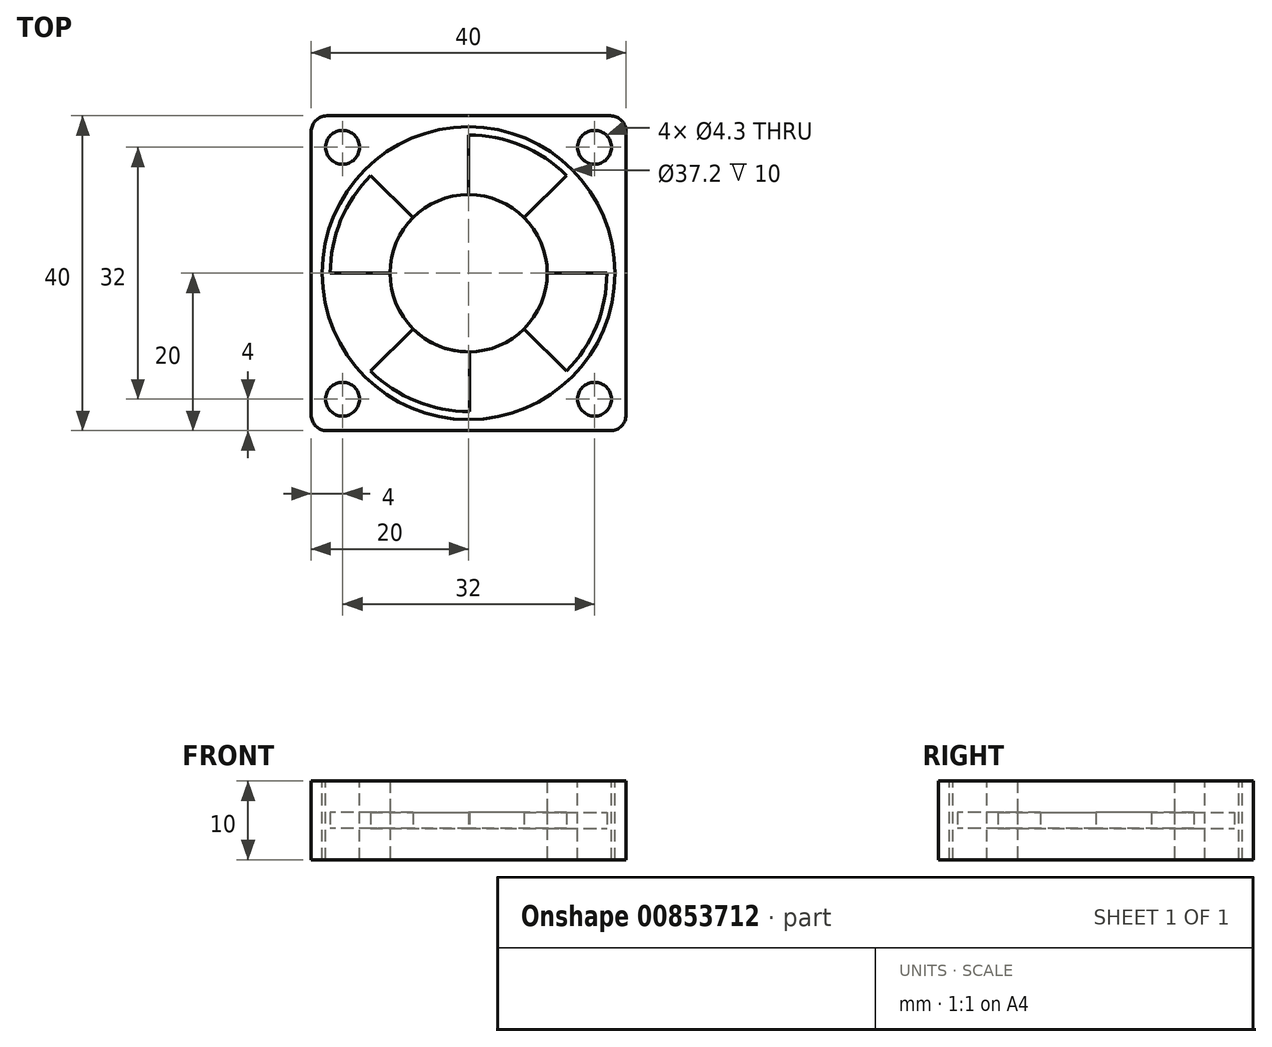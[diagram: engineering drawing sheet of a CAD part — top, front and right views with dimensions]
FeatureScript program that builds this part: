
annotation { "Feature Type Name" : "Feature", "Feature Type Description" : "" }
export const myFeature = defineFeature(function(context is Context, id is Id, definition is map)
    precondition{}
    {
        {
            var Q0;
            Q0=qCreatedBy(makeId("Top.planeOp"),FACE);
            var sketch = newSketch(context, id + "F0", { "sketchPlane" : qUnion([Q0])});
            skLineSegment(sketch, "E0.bottom", {"start": v(0, 0) * mm, "end": v(40, 0) * mm});
            skLineSegment(sketch, "E0.top", {"start": v(0, -40) * mm, "end": v(40, -40) * mm});
            skLineSegment(sketch, "E0.left", {"start": v(0, 0) * mm, "end": v(0, -40) * mm});
            skLineSegment(sketch, "E0.right", {"start": v(40, 0) * mm, "end": v(40, -40) * mm});
            skSolve(sketch);
        }
        {
            var Q0;
            Q0 = qSketchRegion(id + "F0", true);
            extrude(context, id + "F1", {"entities" : qUnion([Q0]), "depth" : 10 * mm, "offsetDistance" : 25 * mm});
        }
        {
            var Q0;
            Q0=makeQuery(id+"F1.opExtrude","CAP_FACE",FACE,{"disambiguationData":[OSD([sQuery(id+"F0.wireOp",EDGE,"E0.bottom"),sQuery(id+"F0.wireOp",EDGE,"E0.top"),sQuery(id+"F0.wireOp",EDGE,"E0.left"),sQuery(id+"F0.wireOp",EDGE,"E0.right")])],"isStart":false});
            var sketch = newSketch(context, id + "F2", { "sketchPlane" : qUnion([Q0])});
            skCircle(sketch, "E1", {"center": v(20, -20) * mm, "radius": 18.6 * mm});
            skPoint(sketch, "E1.centerSnap0", {"position": v(0, -20) * mm});
            skPoint(sketch, "E1.centerSnap1", {"position": v(20, -40) * mm});
            skSolve(sketch);
        }
        {
            var Q0;
            Q0 = qSketchRegion(id + "F2", true);
            extrude(context, id + "F3", {"entities" : qUnion([Q0]), "operationType" : NewBodyOperationType.REMOVE, "oppositeDirection" : true, "depth" : 25 * mm, "offsetDistance" : 25 * mm});
        }
        {
            var Q0;
            Q0=qCreatedBy(makeId("Top.planeOp"),FACE);
            var sketch = newSketch(context, id + "F4", { "sketchPlane" : qUnion([Q0])});
            skPoint(sketch, "E2.0", {"position": v(20, -40) * mm});
            skPoint(sketch, "E3.0", {"position": v(40, -20) * mm});
            skCircle(sketch, "E4", {"center": v(20, -20) * mm, "radius": 9.98 * mm});
            skLineSegment(sketch, "E5", {"start": v(20.1, -29.98) * mm, "end": v(20.1, -37.57) * mm});
            skArc(sketch, "E6", {"start": v(32.42, -32.42) * mm, "mid": v(36.23, -26.72) * mm, "end": v(37.57, -20) * mm});
            skLineSegment(sketch, "E7", {"start": v(20, -10.02) * mm, "end": v(20, -2.43) * mm});
            skLineSegment(sketch, "E8", {"start": v(29.98, -20) * mm, "end": v(37.57, -20) * mm});
            skLineSegment(sketch, "E9", {"start": v(10.02, -20) * mm, "end": v(2.43, -20) * mm});
            skLineSegment(sketch, "E10", {"start": v(20, -20) * mm, "end": v(32.42, -32.42) * mm});
            skLineSegment(sketch, "E11", {"start": v(20, -20) * mm, "end": v(32.42, -7.58) * mm});
            skLineSegment(sketch, "E12", {"start": v(20, -20) * mm, "end": v(7.58, -32.42) * mm});
            skLineSegment(sketch, "E13", {"start": v(20, -20) * mm, "end": v(7.58, -7.58) * mm});
            skArc(sketch, "E14.trimOffspring", {"start": v(32.42, -7.58) * mm, "mid": v(26.72, -3.77) * mm, "end": v(20, -2.43) * mm});
            skArc(sketch, "E15.trimOffspring", {"start": v(7.58, -7.58) * mm, "mid": v(3.77, -13.28) * mm, "end": v(2.43, -20) * mm});
            skArc(sketch, "E16.trimOffspring", {"start": v(7.58, -32.42) * mm, "mid": v(13.33, -36.25) * mm, "end": v(20.1, -37.57) * mm});
            skSolve(sketch);
        }
        {
            var Q0;
            Q0 = qSketchRegion(id + "F4", true);
            var Q1;
            Q1=makeQuery(id+"F1.opExtrude","CAP_FACE",FACE,{"disambiguationData":[OSD([sQuery(id+"F0.wireOp",EDGE,"E0.bottom"),sQuery(id+"F0.wireOp",EDGE,"E0.top"),sQuery(id+"F0.wireOp",EDGE,"E0.left"),sQuery(id+"F0.wireOp",EDGE,"E0.right")])],"isStart":false});
            extrude(context, id + "F5", {"entities" : qUnion([Q0]), "operationType" : NewBodyOperationType.ADD, "endBound" : BoundingType.UP_TO_SURFACE, "depth" : 25 * mm, "endBoundEntityFace" : qUnion([Q1]), "offsetDistance" : 25 * mm});
        }
        {
            var Q0;
            Q0=makeQuery(id+"F1.opExtrude","CAP_FACE",FACE,{"disambiguationData":[OSD([sQuery(id+"F0.wireOp",EDGE,"E0.bottom"),sQuery(id+"F0.wireOp",EDGE,"E0.top"),sQuery(id+"F0.wireOp",EDGE,"E0.left"),sQuery(id+"F0.wireOp",EDGE,"E0.right")])],"isStart":false});
            var sketch = newSketch(context, id + "F6", { "sketchPlane" : qUnion([Q0])});
            skPoint(sketch, "E17.0", {"position": v(20, 0) * mm});
            skLineSegment(sketch, "E18", {"start": v(4, 3.66) * mm, "end": v(4, -45.69) * mm, "construction": true});
            skLineSegment(sketch, "E19", {"start": v(-2.3, -4) * mm, "end": v(43.61, -4) * mm, "construction": true});
            skPoint(sketch, "E20.0", {"position": v(0, -20) * mm});
            skLineSegment(sketch, "E21", {"start": v(-0.82, -20) * mm, "end": v(54, -20) * mm, "construction": true});
            skCircle(sketch, "E22", {"center": v(4, -4) * mm, "radius": 2.15 * mm});
            skCircle(sketch, "E23.MirrorC", {"center": v(4, -36) * mm, "radius": 2.15 * mm});
            skCircle(sketch, "E24.MirrorC", {"center": v(36, -4) * mm, "radius": 2.15 * mm});
            skCircle(sketch, "E25.MirrorC", {"center": v(36, -36) * mm, "radius": 2.15 * mm});
            skSolve(sketch);
        }
        {
            var Q0;
            Q0 = qSketchRegion(id + "F6", true);
            extrude(context, id + "F7", {"entities" : qUnion([Q0]), "operationType" : NewBodyOperationType.REMOVE, "oppositeDirection" : true, "depth" : 25 * mm, "offsetDistance" : 25 * mm});
        }
        {
            var Q0;
            Q0=makeQuery(id+"F1.opExtrude","SWEPT_EDGE",EDGE,{"disambiguationData":[OSD([sQuery(id+"F0.wireOp",EDGE,"E0.bottom"),sQuery(id+"F0.wireOp",EDGE,"E0.left")])]});
            var Q1;
            Q1=makeQuery(id+"F1.opExtrude","SWEPT_EDGE",EDGE,{"disambiguationData":[OSD([sQuery(id+"F0.wireOp",EDGE,"E0.bottom"),sQuery(id+"F0.wireOp",EDGE,"E0.right")])]});
            var Q2;
            Q2=makeQuery(id+"F1.opExtrude","SWEPT_EDGE",EDGE,{"disambiguationData":[OSD([sQuery(id+"F0.wireOp",EDGE,"E0.top"),sQuery(id+"F0.wireOp",EDGE,"E0.right")])]});
            var Q3;
            Q3=makeQuery(id+"F1.opExtrude","SWEPT_EDGE",EDGE,{"disambiguationData":[OSD([sQuery(id+"F0.wireOp",EDGE,"E0.top"),sQuery(id+"F0.wireOp",EDGE,"E0.left")])]});
            fillet(context, id + "F8", {"entities" : qUnion([Q0, Q1, Q2, Q3]), "radius" : 2 * mm, "tangentPropagation" : true, "allowEdgeOverflow" : false});
        }
        {
            var Q0;
            Q0=makeQuery(id+"F5.opExtrude","CAP_FACE",FACE,{"disambiguationData":[OSD([sQuery(id+"F4.wireOp",EDGE,"E4"),sQuery(id+"F4.wireOp",EDGE,"E5"),sQuery(id+"F4.wireOp",EDGE,"E6"),sQuery(id+"F4.wireOp",EDGE,"E7"),sQuery(id+"F4.wireOp",EDGE,"E8"),sQuery(id+"F4.wireOp",EDGE,"E9"),sQuery(id+"F4.wireOp",EDGE,"E10"),sQuery(id+"F4.wireOp",EDGE,"E11"),sQuery(id+"F4.wireOp",EDGE,"E12"),sQuery(id+"F4.wireOp",EDGE,"E13"),sQuery(id+"F4.wireOp",EDGE,"E14.trimOffspring"),sQuery(id+"F4.wireOp",EDGE,"E15.trimOffspring"),sQuery(id+"F4.wireOp",EDGE,"E16.trimOffspring")])],"isStart":false});
            var sketch = newSketch(context, id + "F9", { "sketchPlane" : qUnion([Q0])});
            skLineSegment(sketch, "E26.0.0", {"start": v(20, -2.43) * mm, "end": v(20, -10.02) * mm});
            skArc(sketch, "E26.0.1", {"start": v(20, -10.02) * mm, "mid": v(16.18, -10.78) * mm, "end": v(12.94, -12.94) * mm});
            skLineSegment(sketch, "E26.0.2", {"start": v(12.94, -12.94) * mm, "end": v(7.58, -7.58) * mm});
            skArc(sketch, "E26.0.3", {"start": v(7.58, -7.58) * mm, "mid": v(3.77, -13.28) * mm, "end": v(2.43, -20) * mm});
            skLineSegment(sketch, "E26.0.4", {"start": v(2.43, -20) * mm, "end": v(10.02, -20) * mm});
            skArc(sketch, "E26.0.5", {"start": v(10.02, -20) * mm, "mid": v(10.78, -23.82) * mm, "end": v(12.94, -27.06) * mm});
            skLineSegment(sketch, "E26.0.6", {"start": v(12.94, -27.06) * mm, "end": v(7.58, -32.42) * mm});
            skArc(sketch, "E26.0.7", {"start": v(7.58, -32.42) * mm, "mid": v(13.33, -36.25) * mm, "end": v(20.1, -37.57) * mm});
            skLineSegment(sketch, "E26.0.8", {"start": v(20.1, -37.57) * mm, "end": v(20.1, -29.98) * mm});
            skArc(sketch, "E26.0.9", {"start": v(20.1, -29.98) * mm, "mid": v(23.87, -29.2) * mm, "end": v(27.06, -27.06) * mm});
            skLineSegment(sketch, "E26.0.10", {"start": v(27.06, -27.06) * mm, "end": v(32.42, -32.42) * mm});
            skArc(sketch, "E26.0.11", {"start": v(32.42, -32.42) * mm, "mid": v(36.23, -26.72) * mm, "end": v(37.57, -20) * mm});
            skLineSegment(sketch, "E26.0.12", {"start": v(37.57, -20) * mm, "end": v(29.98, -20) * mm});
            skArc(sketch, "E26.0.13", {"start": v(29.98, -20) * mm, "mid": v(29.22, -16.18) * mm, "end": v(27.06, -12.94) * mm});
            skLineSegment(sketch, "E26.0.14", {"start": v(27.06, -12.94) * mm, "end": v(32.42, -7.58) * mm});
            skArc(sketch, "E26.0.15", {"start": v(32.42, -7.58) * mm, "mid": v(26.72, -3.77) * mm, "end": v(20, -2.43) * mm});
            skCircle(sketch, "E27", {"center": v(20, -20) * mm, "radius": 9.98 * mm});
            skSolve(sketch);
        }
        {
            var Q0;
            {var subQ0=sQuery(id+"F9.wireOp",EDGE,"E26.0.10");Q0=makeQuery(id+"F9.imprint","IMPRINT",FACE,{"disambiguationData":[TD([[makeQuery(id+"F9.imprint","IMPRINT",EDGE,{"derivedFrom":subQ0}),1.0]])]});}
            var Q1;
            {var subQ0=sQuery(id+"F9.wireOp",EDGE,"E26.0.6");Q1=makeQuery(id+"F9.imprint","IMPRINT",FACE,{"disambiguationData":[TD([[makeQuery(id+"F9.imprint","IMPRINT",EDGE,{"derivedFrom":subQ0}),1.0]])]});}
            var Q2;
            {var subQ0=sQuery(id+"F9.wireOp",EDGE,"E26.0.2");Q2=makeQuery(id+"F9.imprint","IMPRINT",FACE,{"disambiguationData":[TD([[makeQuery(id+"F9.imprint","IMPRINT",EDGE,{"derivedFrom":subQ0}),1.0]])]});}
            var Q3;
            {var subQ0=sQuery(id+"F9.wireOp",EDGE,"E26.0.0");Q3=makeQuery(id+"F9.imprint","IMPRINT",FACE,{"disambiguationData":[TD([[makeQuery(id+"F9.imprint","IMPRINT",EDGE,{"derivedFrom":subQ0}),-1.0]])]});}
            extrude(context, id + "F10", {"entities" : qUnion([Q0, Q1, Q2, Q3]), "operationType" : NewBodyOperationType.REMOVE, "oppositeDirection" : true, "depth" : 4 * mm, "offsetDistance" : 25 * mm});
        }
        {
            var Q0;
            Q0=makeQuery(id+"F5.opExtrude","CAP_FACE",FACE,{"disambiguationData":[OSD([sQuery(id+"F4.wireOp",EDGE,"E4"),sQuery(id+"F4.wireOp",EDGE,"E5"),sQuery(id+"F4.wireOp",EDGE,"E6"),sQuery(id+"F4.wireOp",EDGE,"E7"),sQuery(id+"F4.wireOp",EDGE,"E8"),sQuery(id+"F4.wireOp",EDGE,"E9"),sQuery(id+"F4.wireOp",EDGE,"E10"),sQuery(id+"F4.wireOp",EDGE,"E11"),sQuery(id+"F4.wireOp",EDGE,"E12"),sQuery(id+"F4.wireOp",EDGE,"E13"),sQuery(id+"F4.wireOp",EDGE,"E14.trimOffspring"),sQuery(id+"F4.wireOp",EDGE,"E15.trimOffspring"),sQuery(id+"F4.wireOp",EDGE,"E16.trimOffspring")])],"isStart":true});
            var sketch = newSketch(context, id + "F11", { "sketchPlane" : qUnion([Q0])});
            skLineSegment(sketch, "E28.0.0", {"start": v(20, 10.02) * mm, "end": v(20, 2.43) * mm});
            skArc(sketch, "E28.0.1", {"start": v(20, 2.43) * mm, "mid": v(26.72, 3.77) * mm, "end": v(32.42, 7.58) * mm});
            skLineSegment(sketch, "E28.0.2", {"start": v(32.42, 7.58) * mm, "end": v(27.06, 12.94) * mm});
            skArc(sketch, "E28.0.3", {"start": v(27.06, 12.94) * mm, "mid": v(29.22, 16.18) * mm, "end": v(29.98, 20) * mm});
            skLineSegment(sketch, "E28.0.4", {"start": v(29.98, 20) * mm, "end": v(37.57, 20) * mm});
            skArc(sketch, "E28.0.5", {"start": v(37.57, 20) * mm, "mid": v(36.23, 26.72) * mm, "end": v(32.42, 32.42) * mm});
            skLineSegment(sketch, "E28.0.6", {"start": v(32.42, 32.42) * mm, "end": v(27.06, 27.06) * mm});
            skArc(sketch, "E28.0.7", {"start": v(27.06, 27.06) * mm, "mid": v(23.87, 29.2) * mm, "end": v(20.1, 29.98) * mm});
            skLineSegment(sketch, "E28.0.8", {"start": v(20.1, 29.98) * mm, "end": v(20.1, 37.57) * mm});
            skArc(sketch, "E28.0.9", {"start": v(20.1, 37.57) * mm, "mid": v(13.33, 36.25) * mm, "end": v(7.58, 32.42) * mm});
            skLineSegment(sketch, "E28.0.10", {"start": v(7.58, 32.42) * mm, "end": v(12.94, 27.06) * mm});
            skArc(sketch, "E28.0.11", {"start": v(12.94, 27.06) * mm, "mid": v(10.78, 23.82) * mm, "end": v(10.02, 20) * mm});
            skLineSegment(sketch, "E28.0.12", {"start": v(10.02, 20) * mm, "end": v(2.43, 20) * mm});
            skArc(sketch, "E28.0.13", {"start": v(2.43, 20) * mm, "mid": v(3.77, 13.28) * mm, "end": v(7.58, 7.58) * mm});
            skLineSegment(sketch, "E28.0.14", {"start": v(7.58, 7.58) * mm, "end": v(12.94, 12.94) * mm});
            skArc(sketch, "E28.0.15", {"start": v(12.94, 12.94) * mm, "mid": v(16.18, 10.78) * mm, "end": v(20, 10.02) * mm});
            skCircle(sketch, "E29", {"center": v(20, 20) * mm, "radius": 9.98 * mm});
            skSolve(sketch);
        }
        {
            var Q0;
            {var subQ0=sQuery(id+"F11.wireOp",EDGE,"E28.0.12");Q0=makeQuery(id+"F11.imprint","IMPRINT",FACE,{"disambiguationData":[TD([[makeQuery(id+"F11.imprint","IMPRINT",EDGE,{"derivedFrom":subQ0}),1.0]])]});}
            var Q1;
            {var subQ0=sQuery(id+"F11.wireOp",EDGE,"E28.0.8");Q1=makeQuery(id+"F11.imprint","IMPRINT",FACE,{"disambiguationData":[TD([[makeQuery(id+"F11.imprint","IMPRINT",EDGE,{"derivedFrom":subQ0}),1.0]])]});}
            var Q2;
            {var subQ0=sQuery(id+"F11.wireOp",EDGE,"E28.0.4");Q2=makeQuery(id+"F11.imprint","IMPRINT",FACE,{"disambiguationData":[TD([[makeQuery(id+"F11.imprint","IMPRINT",EDGE,{"derivedFrom":subQ0}),1.0]])]});}
            var Q3;
            {var subQ0=sQuery(id+"F11.wireOp",EDGE,"E28.0.0");Q3=makeQuery(id+"F11.imprint","IMPRINT",FACE,{"disambiguationData":[TD([[makeQuery(id+"F11.imprint","IMPRINT",EDGE,{"derivedFrom":subQ0}),1.0]])]});}
            extrude(context, id + "F12", {"entities" : qUnion([Q0, Q1, Q2, Q3]), "operationType" : NewBodyOperationType.REMOVE, "oppositeDirection" : true, "depth" : 4 * mm, "offsetDistance" : 25 * mm});
        }
    });
